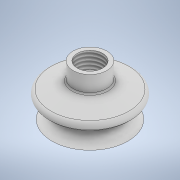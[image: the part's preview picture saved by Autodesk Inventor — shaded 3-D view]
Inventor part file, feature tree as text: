
AUTODESK INVENTOR PART (.ipt)
format: ipt  version: 2022 (Build 260153000, 153)  size: 212,992 bytes
history: native  units: mm
features: sketch x5, extrude x3, fillet x3, chamfer x2, other x1, revolve x1, hole x1
ambient origin geometry x8: Origin, YZ Plane, XZ Plane, XY Plane, X Axis, Y Axis, Z Axis, Center Point
bodies: Body1 (feature_tree)
feature tree (16):
  other  "Sólido1"
  extrude  "Extrusión1"  Depth=10.0mm TaperAngle=0.0deg
  extrude  "Extrusión2"  Depth=10.0mm TaperAngle=0.0deg
  extrude  "Extrusión3"  Depth=10.0mm TaperAngle=0.0deg
  chamfer  "Chaflán1"  Distance=15.0mm Angle=45.0deg
  chamfer  "Chaflán2"  Distance=2.5mm Angle=45.0deg
  fillet  "Empalme1"  Radius=2.5mm
  revolve  "Revolución1"  Angle=90.0deg
  fillet  "Empalme2"  Radius=2.0mm
  hole  "Agujero1"  [1 undecoded]
  fillet  "Empalme3"  [1 undecoded]
  sketch  "Boceto1"  dims[d0=45.0mm d1=10.0mm d2=0.0mm]
  sketch  "Boceto2"  dims[d3=50.0mm d4=10.0mm d5=0.0mm]
  sketch  "Boceto3"  dims[d6=20.0mm d7=10.0mm d8=0.0mm d9=15.0mm d10=5.0mm d11=45.0deg d12=2.5mm d13=7.75mm d14=45.0deg d15=2.5mm]
  sketch  "Boceto5"  dims[d16=5.0mm d17=90.0deg d18=2.0mm]
  sketch  "Boceto6"  dims[d19=15.1638mm d20=10.0mm d21=4.0mm d22=2.0mm d23=90.0deg d24=8.0mm d25=20.594885mm d26=1.0mm]
note: 2 required parameter values undecoded (feature->parameter linkage not recoverable at this tier; creation-order binding heuristic only, values carry confidence <= 0.55)
